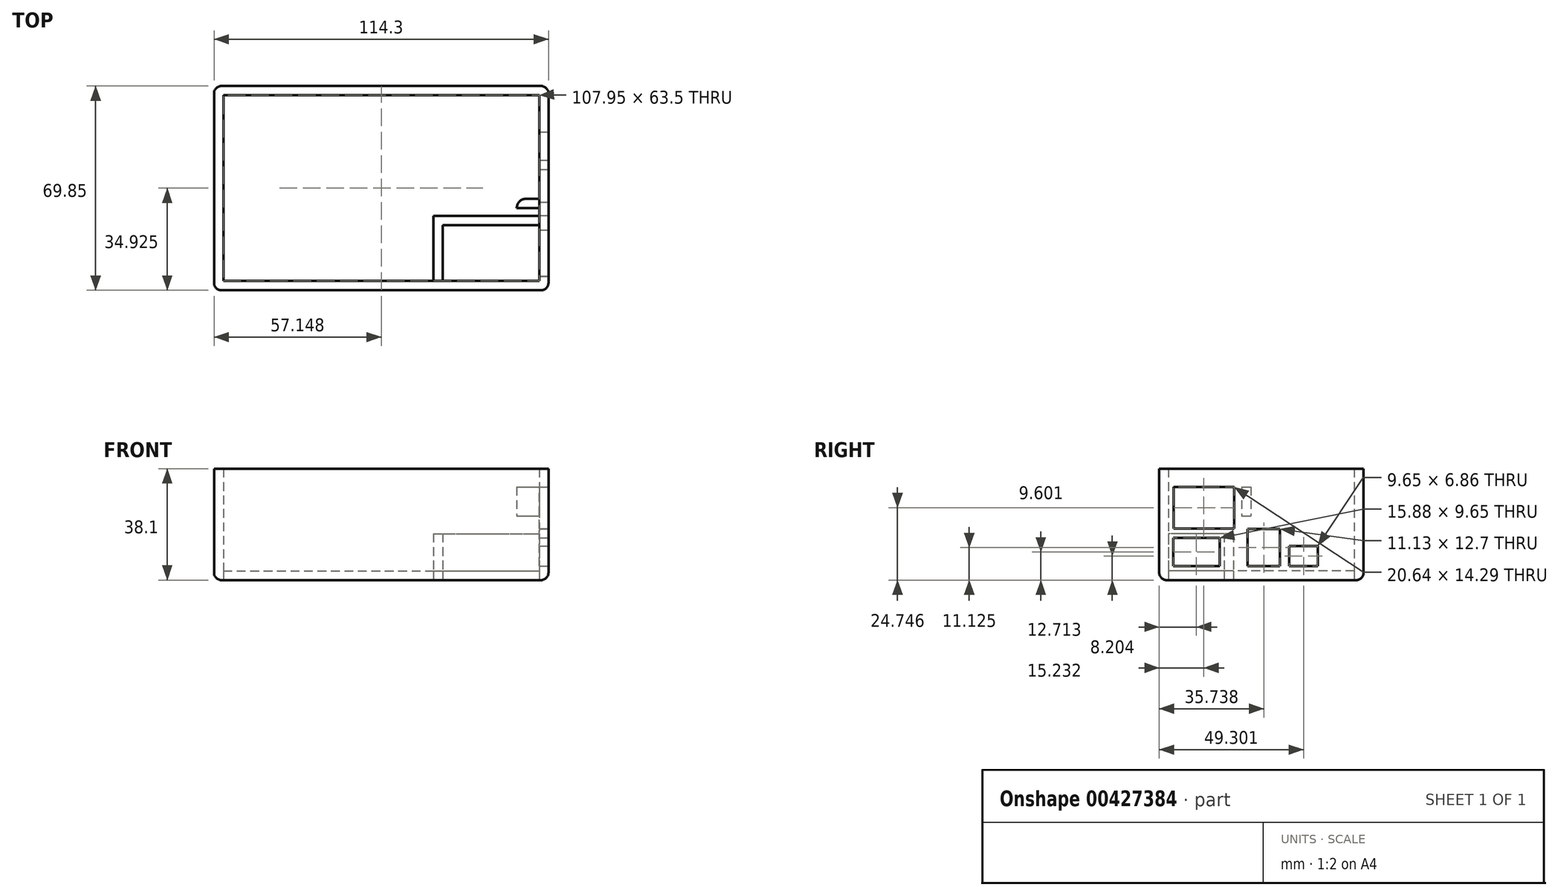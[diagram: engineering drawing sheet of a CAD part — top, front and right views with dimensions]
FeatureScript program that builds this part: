
annotation { "Feature Type Name" : "Feature", "Feature Type Description" : "" }
export const myFeature = defineFeature(function(context is Context, id is Id, definition is map)
    precondition{}
    {
        {
            var Q0;
            Q0=qCreatedBy(makeId("Top.planeOp"),FACE);
            var sketch = newSketch(context, id + "F0", { "sketchPlane" : qUnion([Q0])});
            skLineSegment(sketch, "E0.bottom", {"start": v(-70.41, 44.45) * mm, "end": v(43.89, 44.45) * mm});
            skLineSegment(sketch, "E0.top", {"start": v(-70.41, -25.4) * mm, "end": v(43.89, -25.4) * mm});
            skLineSegment(sketch, "E0.left", {"start": v(-70.41, 44.45) * mm, "end": v(-70.41, -25.4) * mm});
            skLineSegment(sketch, "E0.right", {"start": v(43.89, 0) * mm, "end": v(43.89, -25.4) * mm});
            skLineSegment(sketch, "E1", {"start": v(40.71, 41.28) * mm, "end": v(40.71, -22.23) * mm});
            skLineSegment(sketch, "E2", {"start": v(7.7, 41.28) * mm, "end": v(7.7, 0) * mm});
            skLineSegment(sketch, "E3", {"start": v(-67.24, 41.28) * mm, "end": v(-67.24, -22.23) * mm});
            skLineSegment(sketch, "E4", {"start": v(-67.24, -22.23) * mm, "end": v(4.52, -22.23) * mm});
            skLineSegment(sketch, "E5", {"start": v(-67.24, 41.28) * mm, "end": v(4.52, 41.28) * mm});
            skLineSegment(sketch, "E6", {"start": v(7.7, 0) * mm, "end": v(40.71, 0) * mm});
            skLineSegment(sketch, "E7", {"start": v(7.7, -3.18) * mm, "end": v(40.71, -3.18) * mm});
            skPoint(sketch, "E8.orphan", {"position": v(-70.41, 0) * mm});
            skPoint(sketch, "E9.orphan", {"position": v(-3.74, -25.4) * mm});
            skPoint(sketch, "E10.orphan", {"position": v(7.7, -25.4) * mm});
            skLineSegment(sketch, "E11", {"start": v(43.89, 0) * mm, "end": v(43.89, 44.45) * mm});
            skLineSegment(sketch, "E12", {"start": v(43.89, 44.45) * mm, "end": v(43.89, 44.45) * mm});
            skPoint(sketch, "E13.end.orphan", {"position": v(42.3, 0) * mm});
            skPoint(sketch, "E14.start.orphan", {"position": v(4.52, 41.28) * mm});
            skLineSegment(sketch, "E15", {"start": v(4.52, 41.28) * mm, "end": v(4.52, -22.23) * mm});
            skLineSegment(sketch, "E16.trimOffspring", {"start": v(7.7, 41.28) * mm, "end": v(40.71, 41.28) * mm});
            skLineSegment(sketch, "E17.trimOffspring", {"start": v(7.7, -3.18) * mm, "end": v(7.7, -22.23) * mm});
            skLineSegment(sketch, "E18.trimOffspring", {"start": v(7.7, -22.23) * mm, "end": v(40.71, -22.23) * mm});
            skLineSegment(sketch, "E19", {"start": v(7.7, 41.28) * mm, "end": v(4.52, 41.28) * mm});
            skLineSegment(sketch, "E20", {"start": v(4.52, -22.23) * mm, "end": v(7.7, -22.23) * mm});
            skLineSegment(sketch, "E21", {"start": v(7.7, 0) * mm, "end": v(4.52, 0) * mm});
            skSolve(sketch);
        }
        {
            var Q0;
            {var subQ0=sQuery(id+"F0.wireOp",EDGE,"E14");Q0=makeQuery(id+"F0.imprint","IMPRINT",FACE,{"disambiguationData":[TD([[makeQuery(id+"F0.imprint","IMPRINT",EDGE,{"derivedFrom":subQ0}),-1.0]])]});}
            var Q1;
            {var subQ3=sQuery(id+"F0.wireOp",EDGE,"E6");Q1=makeQuery(id+"F0.imprint","IMPRINT",FACE,{"disambiguationData":[TD([[makeQuery(id+"F0.imprint","IMPRINT",EDGE,{"derivedFrom":subQ3}),1.0]])]});}
            var Q2;
            {var subQ3=sQuery(id+"F0.wireOp",EDGE,"E7");Q2=makeQuery(id+"F0.imprint","IMPRINT",FACE,{"disambiguationData":[TD([[makeQuery(id+"F0.imprint","IMPRINT",EDGE,{"derivedFrom":subQ3}),-1.0]])]});}
            var Q3;
            Q3=makeQuery(id+"F0.imprint","IMPRINT",FACE,{"disambiguationData":[TD([[makeQuery(id+"F0.imprint","IMPRINT",EDGE,{"derivedFrom":sQuery(id+"F0.wireOp",EDGE,"E3")}),1.0]])]});
            var Q4;
            Q4=makeQuery(id+"F0.imprint","IMPRINT",FACE,{"disambiguationData":[TD([[makeQuery(id+"F0.imprint","IMPRINT",EDGE,{"derivedFrom":sQuery(id+"F0.wireOp",EDGE,"E2")}),-1.0]])]});
            extrude(context, id + "F1", {"entities" : qUnion([Q0, Q1, Q2, Q3, Q4]), "depth" : 3.17 * mm});
        }
        {
            var Q0;
            {var subQ0=sQuery(id+"F0.wireOp",EDGE,"E14");Q0=makeQuery(id+"F0.imprint","IMPRINT",FACE,{"disambiguationData":[TD([[makeQuery(id+"F0.imprint","IMPRINT",EDGE,{"derivedFrom":subQ0}),1.0]])]});}
            var Q1;
            {var subQ0=sQuery(id+"F0.wireOp",EDGE,"E6");Q1=makeQuery(id+"F0.imprint","IMPRINT",FACE,{"disambiguationData":[TD([[makeQuery(id+"F0.imprint","IMPRINT",EDGE,{"derivedFrom":subQ0}),-1.0]])]});}
            extrude(context, id + "F2", {"entities" : qUnion([Q0, Q1]), "depth" : 15.88 * mm});
        }
        {
            var Q0;
            Q0=makeQuery(id+"F0.imprint","IMPRINT",FACE,{"disambiguationData":[TD([[makeQuery(id+"F0.imprint","IMPRINT",EDGE,{"derivedFrom":sQuery(id+"F0.wireOp",EDGE,"E0.bottom")}),-1.0]])]});
            extrude(context, id + "F3", {"entities" : qUnion([Q0]), "depth" : 38.1 * mm});
        }
        {
            var Q0;
            Q0=makeQuery(id+"F3.opExtrude","SWEPT_FACE",FACE,{"disambiguationData":[OSD([sQuery(id+"F0.wireOp",EDGE,"E0.right")])]});
            var sketch = newSketch(context, id + "F4", { "sketchPlane" : qUnion([Q0])});
            skLineSegment(sketch, "E22.bottom", {"start": v(-25.4, 38.1) * mm, "end": v(38.1, 38.1) * mm});
            skLineSegment(sketch, "E22.top", {"start": v(-25.4, 0) * mm, "end": v(44.45, 0) * mm});
            skLineSegment(sketch, "E22.left", {"start": v(-25.4, 38.1) * mm, "end": v(-25.4, 0) * mm});
            skLineSegment(sketch, "E22.right", {"start": v(44.45, 38.1) * mm, "end": v(44.45, 0) * mm});
            skLineSegment(sketch, "E23.bottom", {"start": v(-20.62, 4.78) * mm, "end": v(-4.75, 4.78) * mm});
            skLineSegment(sketch, "E23.top", {"start": v(-20.62, 14.43) * mm, "end": v(-4.75, 14.43) * mm});
            skLineSegment(sketch, "E23.left", {"start": v(-20.62, 4.78) * mm, "end": v(-20.62, 14.43) * mm});
            skLineSegment(sketch, "E23.right", {"start": v(-4.75, 4.78) * mm, "end": v(-4.75, 14.43) * mm});
            skLineSegment(sketch, "E24.bottom", {"start": v(28.73, 4.78) * mm, "end": v(19.08, 4.78) * mm});
            skLineSegment(sketch, "E24.top", {"start": v(28.73, 11.63) * mm, "end": v(19.08, 11.63) * mm});
            skLineSegment(sketch, "E24.left", {"start": v(28.73, 4.78) * mm, "end": v(28.73, 11.63) * mm});
            skLineSegment(sketch, "E24.right", {"start": v(19.08, 4.78) * mm, "end": v(19.08, 11.63) * mm});
            skLineSegment(sketch, "E25.bottom", {"start": v(15.9, 4.78) * mm, "end": v(4.78, 4.78) * mm});
            skLineSegment(sketch, "E25.top", {"start": v(15.9, 17.48) * mm, "end": v(4.78, 17.48) * mm});
            skLineSegment(sketch, "E25.left", {"start": v(15.9, 4.78) * mm, "end": v(15.9, 17.48) * mm});
            skLineSegment(sketch, "E25.right", {"start": v(4.78, 4.78) * mm, "end": v(4.78, 17.48) * mm});
            skLineSegment(sketch, "E26.bottom", {"start": v(-20.49, 17.6) * mm, "end": v(0.15, 17.6) * mm});
            skLineSegment(sketch, "E26.top", {"start": v(-20.49, 31.89) * mm, "end": v(0.15, 31.89) * mm});
            skLineSegment(sketch, "E26.left", {"start": v(-20.49, 17.6) * mm, "end": v(-20.49, 31.89) * mm});
            skLineSegment(sketch, "E26.right", {"start": v(0.15, 17.6) * mm, "end": v(0.15, 31.89) * mm});
            skSolve(sketch);
        }
        {
            var Q0;
            Q0=makeQuery(id+"F4.imprint","IMPRINT",FACE,{"disambiguationData":[TD([[makeQuery(id+"F4.imprint","IMPRINT",EDGE,{"derivedFrom":sQuery(id+"F4.wireOp",EDGE,"E23.bottom")}),1.0]])]});
            var Q1;
            Q1=makeQuery(id+"F4.imprint","IMPRINT",FACE,{"disambiguationData":[TD([[makeQuery(id+"F4.imprint","IMPRINT",EDGE,{"derivedFrom":sQuery(id+"F4.wireOp",EDGE,"E25.bottom")}),-1.0]])]});
            var Q2;
            Q2=makeQuery(id+"F4.imprint","IMPRINT",FACE,{"disambiguationData":[TD([[makeQuery(id+"F4.imprint","IMPRINT",EDGE,{"derivedFrom":sQuery(id+"F4.wireOp",EDGE,"E24.bottom")}),-1.0]])]});
            var Q3;
            Q3=makeQuery(id+"F4.imprint","IMPRINT",FACE,{"disambiguationData":[TD([[makeQuery(id+"F4.imprint","IMPRINT",EDGE,{"derivedFrom":sQuery(id+"F4.wireOp",EDGE,"E26.bottom")}),1.0]])]});
            extrude(context, id + "F5", {"entities" : qUnion([Q0, Q1, Q2, Q3]), "operationType" : NewBodyOperationType.REMOVE, "oppositeDirection" : true, "depth" : 6.6 * mm});
        }
        {
            var Q0;
            Q0=makeQuery(id+"F3.opExtrude","SWEPT_FACE",FACE,{"disambiguationData":[OSD([sQuery(id+"F0.wireOp",EDGE,"E1")])]});
            var sketch = newSketch(context, id + "F6", { "sketchPlane" : qUnion([Q0])});
            skLineSegment(sketch, "E27.bottom", {"start": v(-2.7, 31.89) * mm, "end": v(-5.87, 31.89) * mm});
            skLineSegment(sketch, "E27.top", {"start": v(-2.7, 21.94) * mm, "end": v(-5.87, 21.94) * mm});
            skLineSegment(sketch, "E27.left", {"start": v(-2.7, 31.89) * mm, "end": v(-2.7, 21.94) * mm});
            skLineSegment(sketch, "E27.right", {"start": v(-5.87, 31.89) * mm, "end": v(-5.87, 21.94) * mm});
            skSolve(sketch);
        }
        {
            var Q0;
            Q0=makeQuery(id+"F6.imprint","IMPRINT",FACE,{"disambiguationData":[TD([[makeQuery(id+"F6.imprint","IMPRINT",EDGE,{"derivedFrom":sQuery(id+"F6.wireOp",EDGE,"E27.bottom")}),1.0]])]});
            extrude(context, id + "F7", {"entities" : qUnion([Q0]), "operationType" : NewBodyOperationType.ADD, "depth" : 7.62 * mm});
        }
        {
            var Q0;
            Q0=makeQuery(id+"F7.opExtrude","CAP_EDGE",EDGE,{"disambiguationData":[OSD([sQuery(id+"F6.wireOp",EDGE,"E27.right")])],"isStart":false});
            fillet(context, id + "F8", {"entities" : qUnion([Q0]), "radius" : 3 * mm, "tangentPropagation" : true, "allowEdgeOverflow" : false});
        }
        {
            var Q0;
            Q0=makeQuery(id+"F3.opExtrude","SWEPT_EDGE",EDGE,{"disambiguationData":[OSD([sQuery(id+"F0.wireOp",EDGE,"E0.bottom"),sQuery(id+"F0.wireOp",EDGE,"E0.left")])]});
            fillet(context, id + "F9", {"entities" : qUnion([Q0]), "radius" : 2.5 * mm, "tangentPropagation" : true, "allowEdgeOverflow" : false});
        }
        {
            var Q0;
            Q0=makeQuery(id+"F3.opExtrude","SWEPT_EDGE",EDGE,{"disambiguationData":[OSD([sQuery(id+"F0.wireOp",EDGE,"E0.bottom"),sQuery(id+"F0.wireOp",EDGE,"E11")])]});
            fillet(context, id + "F10", {"entities" : qUnion([Q0]), "radius" : 2.5 * mm, "tangentPropagation" : true, "allowEdgeOverflow" : false});
        }
        {
            var Q0;
            Q0=makeQuery(id+"F3.opExtrude","SWEPT_EDGE",EDGE,{"disambiguationData":[OSD([sQuery(id+"F0.wireOp",EDGE,"E0.top"),sQuery(id+"F0.wireOp",EDGE,"E0.right")])]});
            fillet(context, id + "F11", {"entities" : qUnion([Q0]), "radius" : 2.5 * mm, "tangentPropagation" : true, "allowEdgeOverflow" : false});
        }
        {
            var Q0;
            Q0=makeQuery(id+"F3.opExtrude","SWEPT_EDGE",EDGE,{"disambiguationData":[OSD([sQuery(id+"F0.wireOp",EDGE,"E0.top"),sQuery(id+"F0.wireOp",EDGE,"E0.left")])]});
            fillet(context, id + "F12", {"entities" : qUnion([Q0]), "radius" : 2.5 * mm, "tangentPropagation" : true, "allowEdgeOverflow" : false});
        }
        {
            var Q0;
            Q0=makeQuery(id+"F3.opExtrude","CAP_EDGE",EDGE,{"disambiguationData":[OSD([sQuery(id+"F0.wireOp",EDGE,"E0.top")])],"isStart":true});
            var Q1;
            {var subQ0=sQuery(id+"F0.wireOp",EDGE,"E0.left");var subQ1=sQuery(id+"F0.wireOp",EDGE,"E0.top");Q1=makeQuery(id+"F12.opFillet","BLEND_EDGE",EDGE,{"blendedFrom":[makeQuery(id+"F3.opExtrude","SWEPT_EDGE",EDGE,{"disambiguationData":[OSD([subQ1,subQ0])]}),makeQuery(id+"F3.opExtrude","CAP_FACE",FACE,{"disambiguationData":[OSD([sQuery(id+"F0.wireOp",EDGE,"E0.bottom"),subQ1,subQ0,sQuery(id+"F0.wireOp",EDGE,"E0.right"),sQuery(id+"F0.wireOp",EDGE,"E1"),sQuery(id+"F0.wireOp",EDGE,"E3"),sQuery(id+"F0.wireOp",EDGE,"E4"),sQuery(id+"F0.wireOp",EDGE,"E5"),sQuery(id+"F0.wireOp",EDGE,"E11"),sQuery(id+"F0.wireOp",EDGE,"E16.trimOffspring"),sQuery(id+"F0.wireOp",EDGE,"E18.trimOffspring"),sQuery(id+"F0.wireOp",EDGE,"E19"),sQuery(id+"F0.wireOp",EDGE,"E20")])],"isStart":true})],"blendedInto":[makeQuery(id+"F3.opExtrude","CAP_FACE",FACE,{"disambiguationData":[OSD([sQuery(id+"F0.wireOp",EDGE,"E0.bottom"),subQ1,subQ0,sQuery(id+"F0.wireOp",EDGE,"E0.right"),sQuery(id+"F0.wireOp",EDGE,"E1"),sQuery(id+"F0.wireOp",EDGE,"E3"),sQuery(id+"F0.wireOp",EDGE,"E4"),sQuery(id+"F0.wireOp",EDGE,"E5"),sQuery(id+"F0.wireOp",EDGE,"E11"),sQuery(id+"F0.wireOp",EDGE,"E16.trimOffspring"),sQuery(id+"F0.wireOp",EDGE,"E18.trimOffspring"),sQuery(id+"F0.wireOp",EDGE,"E19"),sQuery(id+"F0.wireOp",EDGE,"E20")])],"isStart":true})]});}
            var Q2;
            Q2=makeQuery(id+"F3.opExtrude","CAP_EDGE",EDGE,{"disambiguationData":[OSD([sQuery(id+"F0.wireOp",EDGE,"E0.left")])],"isStart":true});
            var Q3;
            {var subQ0=sQuery(id+"F0.wireOp",EDGE,"E0.left");var subQ1=sQuery(id+"F0.wireOp",EDGE,"E0.bottom");Q3=makeQuery(id+"F9.opFillet","BLEND_EDGE",EDGE,{"blendedFrom":[makeQuery(id+"F3.opExtrude","SWEPT_EDGE",EDGE,{"disambiguationData":[OSD([subQ1,subQ0])]}),makeQuery(id+"F3.opExtrude","CAP_FACE",FACE,{"disambiguationData":[OSD([subQ1,sQuery(id+"F0.wireOp",EDGE,"E0.top"),subQ0,sQuery(id+"F0.wireOp",EDGE,"E0.right"),sQuery(id+"F0.wireOp",EDGE,"E1"),sQuery(id+"F0.wireOp",EDGE,"E3"),sQuery(id+"F0.wireOp",EDGE,"E4"),sQuery(id+"F0.wireOp",EDGE,"E5"),sQuery(id+"F0.wireOp",EDGE,"E11"),sQuery(id+"F0.wireOp",EDGE,"E16.trimOffspring"),sQuery(id+"F0.wireOp",EDGE,"E18.trimOffspring"),sQuery(id+"F0.wireOp",EDGE,"E19"),sQuery(id+"F0.wireOp",EDGE,"E20")])],"isStart":true})],"blendedInto":[makeQuery(id+"F3.opExtrude","CAP_FACE",FACE,{"disambiguationData":[OSD([subQ1,sQuery(id+"F0.wireOp",EDGE,"E0.top"),subQ0,sQuery(id+"F0.wireOp",EDGE,"E0.right"),sQuery(id+"F0.wireOp",EDGE,"E1"),sQuery(id+"F0.wireOp",EDGE,"E3"),sQuery(id+"F0.wireOp",EDGE,"E4"),sQuery(id+"F0.wireOp",EDGE,"E5"),sQuery(id+"F0.wireOp",EDGE,"E11"),sQuery(id+"F0.wireOp",EDGE,"E16.trimOffspring"),sQuery(id+"F0.wireOp",EDGE,"E18.trimOffspring"),sQuery(id+"F0.wireOp",EDGE,"E19"),sQuery(id+"F0.wireOp",EDGE,"E20")])],"isStart":true})]});}
            var Q4;
            Q4=makeQuery(id+"F3.opExtrude","CAP_EDGE",EDGE,{"disambiguationData":[OSD([sQuery(id+"F0.wireOp",EDGE,"E0.bottom")])],"isStart":true});
            var Q5;
            {var subQ0=sQuery(id+"F0.wireOp",EDGE,"E11");var subQ1=sQuery(id+"F0.wireOp",EDGE,"E0.bottom");Q5=makeQuery(id+"F10.opFillet","BLEND_EDGE",EDGE,{"blendedFrom":[makeQuery(id+"F3.opExtrude","SWEPT_EDGE",EDGE,{"disambiguationData":[OSD([subQ1,subQ0])]}),makeQuery(id+"F3.opExtrude","CAP_FACE",FACE,{"disambiguationData":[OSD([subQ1,sQuery(id+"F0.wireOp",EDGE,"E0.top"),sQuery(id+"F0.wireOp",EDGE,"E0.left"),sQuery(id+"F0.wireOp",EDGE,"E0.right"),sQuery(id+"F0.wireOp",EDGE,"E1"),sQuery(id+"F0.wireOp",EDGE,"E3"),sQuery(id+"F0.wireOp",EDGE,"E4"),sQuery(id+"F0.wireOp",EDGE,"E5"),subQ0,sQuery(id+"F0.wireOp",EDGE,"E16.trimOffspring"),sQuery(id+"F0.wireOp",EDGE,"E18.trimOffspring"),sQuery(id+"F0.wireOp",EDGE,"E19"),sQuery(id+"F0.wireOp",EDGE,"E20")])],"isStart":true})],"blendedInto":[makeQuery(id+"F3.opExtrude","CAP_FACE",FACE,{"disambiguationData":[OSD([subQ1,sQuery(id+"F0.wireOp",EDGE,"E0.top"),sQuery(id+"F0.wireOp",EDGE,"E0.left"),sQuery(id+"F0.wireOp",EDGE,"E0.right"),sQuery(id+"F0.wireOp",EDGE,"E1"),sQuery(id+"F0.wireOp",EDGE,"E3"),sQuery(id+"F0.wireOp",EDGE,"E4"),sQuery(id+"F0.wireOp",EDGE,"E5"),subQ0,sQuery(id+"F0.wireOp",EDGE,"E16.trimOffspring"),sQuery(id+"F0.wireOp",EDGE,"E18.trimOffspring"),sQuery(id+"F0.wireOp",EDGE,"E19"),sQuery(id+"F0.wireOp",EDGE,"E20")])],"isStart":true})]});}
            var Q6;
            Q6=makeQuery(id+"F3.opExtrude","CAP_EDGE",EDGE,{"disambiguationData":[OSD([sQuery(id+"F0.wireOp",EDGE,"E0.right"),sQuery(id+"F0.wireOp",EDGE,"E11")])],"isStart":true});
            var Q7;
            {var subQ0=sQuery(id+"F0.wireOp",EDGE,"E0.right");var subQ1=sQuery(id+"F0.wireOp",EDGE,"E0.top");Q7=makeQuery(id+"F11.opFillet","BLEND_EDGE",EDGE,{"blendedFrom":[makeQuery(id+"F3.opExtrude","SWEPT_EDGE",EDGE,{"disambiguationData":[OSD([subQ1,subQ0])]}),makeQuery(id+"F3.opExtrude","CAP_FACE",FACE,{"disambiguationData":[OSD([sQuery(id+"F0.wireOp",EDGE,"E0.bottom"),subQ1,sQuery(id+"F0.wireOp",EDGE,"E0.left"),subQ0,sQuery(id+"F0.wireOp",EDGE,"E1"),sQuery(id+"F0.wireOp",EDGE,"E3"),sQuery(id+"F0.wireOp",EDGE,"E4"),sQuery(id+"F0.wireOp",EDGE,"E5"),sQuery(id+"F0.wireOp",EDGE,"E11"),sQuery(id+"F0.wireOp",EDGE,"E16.trimOffspring"),sQuery(id+"F0.wireOp",EDGE,"E18.trimOffspring"),sQuery(id+"F0.wireOp",EDGE,"E19"),sQuery(id+"F0.wireOp",EDGE,"E20")])],"isStart":true})],"blendedInto":[makeQuery(id+"F3.opExtrude","CAP_FACE",FACE,{"disambiguationData":[OSD([sQuery(id+"F0.wireOp",EDGE,"E0.bottom"),subQ1,sQuery(id+"F0.wireOp",EDGE,"E0.left"),subQ0,sQuery(id+"F0.wireOp",EDGE,"E1"),sQuery(id+"F0.wireOp",EDGE,"E3"),sQuery(id+"F0.wireOp",EDGE,"E4"),sQuery(id+"F0.wireOp",EDGE,"E5"),sQuery(id+"F0.wireOp",EDGE,"E11"),sQuery(id+"F0.wireOp",EDGE,"E16.trimOffspring"),sQuery(id+"F0.wireOp",EDGE,"E18.trimOffspring"),sQuery(id+"F0.wireOp",EDGE,"E19"),sQuery(id+"F0.wireOp",EDGE,"E20")])],"isStart":true})]});}
            fillet(context, id + "F13", {"entities" : qUnion([Q0, Q1, Q2, Q3, Q4, Q5, Q6, Q7]), "radius" : 2.5 * mm, "tangentPropagation" : true, "allowEdgeOverflow" : false});
        }
    });
